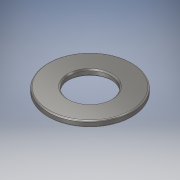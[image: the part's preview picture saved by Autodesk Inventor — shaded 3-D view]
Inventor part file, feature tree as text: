
AUTODESK INVENTOR PART (.ipt)
format: ipt  version: 2019.2 (Build 232265000, 265)  size: 131,584 bytes
history: native  units: mm
features: extrude x1, chamfer x1, fillet x1, sketch x1
ambient origin geometry x8: Origin, YZ Plane, XZ Plane, XY Plane, X Axis, Y Axis, Z Axis, Center Point
bodies: Solid1 (feature_tree)
feature tree (4):
  extrude  "Extrusion1"  Depth=0.1mm
  chamfer  "Chamfer1"  Distance=0.5mm
  fillet  "Fillet1"  Radius=0.1mm
  sketch  "Sketch1"  dims[d0=3.5mm d1=7.0mm d2=0.5mm d3=0.0mm d4=0.1mm d5=2.0mm d6=45.0deg d7=0.1mm]
